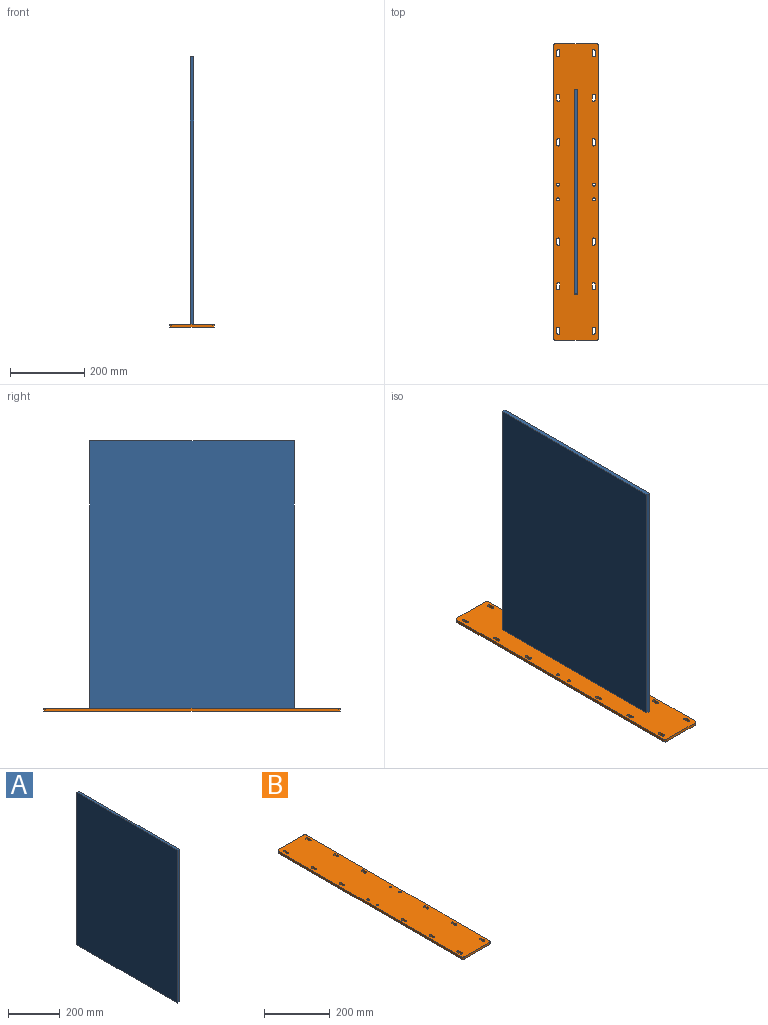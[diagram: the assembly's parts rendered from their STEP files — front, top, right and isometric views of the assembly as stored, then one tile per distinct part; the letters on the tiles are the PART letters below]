
ASSEMBLY  parts=2 mates=1
PART A: 6 faces, bbox 10x550x720 mm
  f0: plane 720x10mm, normal (0,-1,0), area 7200mm2, adj f1,f3,f4,f5
  f1: plane 550x10mm, normal (0,0,1), area 5500mm2, adj f0,f2,f4,f5
  f2: plane 720x10mm, normal (0,1,0), area 7200mm2, adj f1,f3,f4,f5
  f3: plane 550x10mm, normal (0,0,-1), area 5500mm2, adj f0,f2,f4,f5
  f4: plane 720x550mm, normal (-1,0,0), area 396000mm2, adj f0,f1,f2,f3
  f5: plane 720x550mm, normal (1,0,0), area 396000mm2, adj f0,f1,f2,f3
PART B: 62 faces, bbox 120x800x8 mm
  f0: plane 12x8mm, normal (-1,0,0), area 96mm2, adj f1,f30,f31,f32
  f1: cylinder r=4mm len=8mm, axis (0,0,-1), area 100.5mm2, adj f0,f2,f31,f32
  f2: plane 12x8mm, normal (1,0,0), area 96mm2, adj f1,f30,f31,f32
  f3: plane 12x8mm, normal (-1,0,0), area 96mm2, adj f4,f22,f31,f32
  f4: cylinder r=4mm len=8mm, axis (0,0,-1), area 100.5mm2, adj f3,f5,f31,f32
  f5: plane 12x8mm, normal (1,0,0), area 96mm2, adj f4,f22,f31,f32
  f6: plane 12x8mm, normal (-1,0,0), area 96mm2, adj f7,f23,f31,f32
  f7: cylinder r=4mm len=8mm, axis (0,0,-1), area 100.5mm2, adj f6,f8,f31,f32
  f8: plane 12x8mm, normal (1,0,0), area 96mm2, adj f7,f23,f31,f32
  f9: plane 788x8mm, normal (1,0,0), area 6304mm2, adj f10,f31,f32,f42
  f10: cylinder r=6mm len=8mm, axis (0,0,-1), area 75.4mm2, adj f9,f11,f31,f32
  f11: plane 108x8mm, normal (0,1,0), area 864mm2, adj f10,f12,f31,f32
  f12: cylinder r=6mm len=8mm, axis (0,0,-1), area 75.4mm2, adj f11,f24,f31,f32
  f13: plane 12x8mm, normal (-1,0,0), area 96mm2, adj f14,f25,f31,f32
  f14: cylinder r=4mm len=8mm, axis (0,0,-1), area 100.5mm2, adj f13,f15,f31,f32
  f15: plane 12x8mm, normal (1,0,0), area 96mm2, adj f14,f25,f31,f32
  f16: plane 12x8mm, normal (-1,0,0), area 96mm2, adj f17,f26,f31,f32
  f17: cylinder r=4mm len=8mm, axis (0,0,-1), area 100.5mm2, adj f16,f18,f31,f32
  f18: plane 12x8mm, normal (1,0,0), area 96mm2, adj f17,f26,f31,f32
  f19: plane 12x8mm, normal (-1,0,0), area 96mm2, adj f20,f27,f31,f32
  f20: cylinder r=4mm len=8mm, axis (0,0,-1), area 100.5mm2, adj f19,f21,f31,f32
  f21: plane 12x8mm, normal (1,0,0), area 96mm2, adj f20,f27,f31,f32
  f22: cylinder r=4mm len=8mm, axis (0,0,-1), area 100.5mm2, adj f3,f5,f31,f32
  f23: cylinder r=4mm len=8mm, axis (0,0,-1), area 100.5mm2, adj f6,f8,f31,f32
  f24: plane 788x8mm, normal (-1,0,0), area 6304mm2, adj f12,f31,f32,f44
  f25: cylinder r=4mm len=8mm, axis (0,0,-1), area 100.5mm2, adj f13,f15,f31,f32
  f26: cylinder r=4mm len=8mm, axis (0,0,-1), area 100.5mm2, adj f16,f18,f31,f32
  f27: cylinder r=4mm len=8mm, axis (0,0,-1), area 100.5mm2, adj f19,f21,f31,f32
  f28: cylinder r=4mm len=8mm, axis (0,0,-1), area 201.1mm2, adj f31,f32
  f29: cylinder r=4mm len=8mm, axis (0,0,-1), area 201.1mm2, adj f31,f32
  f30: cylinder r=4mm len=8mm, axis (0,0,-1), area 100.5mm2, adj f0,f2,f31,f32
  f31: plane 800x120mm, normal (0,0,1), area 94012.8mm2, adj f0,f1,f2,f3,f4,f5,f6,f7
  f32: plane 800x120mm, normal (0,0,-1), area 94012.8mm2, adj f0,f1,f2,f3,f4,f5,f6,f7
  f33: plane 12x8mm, normal (-1,0,0), area 96mm2, adj f31,f32,f34,f61
  f34: cylinder r=4mm len=8mm, axis (0,0,-1), area 100.5mm2, adj f31,f32,f33,f35
  f35: plane 12x8mm, normal (1,0,0), area 96mm2, adj f31,f32,f34,f61
  f36: plane 12x8mm, normal (-1,0,0), area 96mm2, adj f31,f32,f37,f54
  f37: cylinder r=4mm len=8mm, axis (0,0,-1), area 100.5mm2, adj f31,f32,f36,f38
  f38: plane 12x8mm, normal (1,0,0), area 96mm2, adj f31,f32,f37,f54
  f39: plane 12x8mm, normal (-1,0,0), area 96mm2, adj f31,f32,f40,f55
  f40: cylinder r=4mm len=8mm, axis (0,0,-1), area 100.5mm2, adj f31,f32,f39,f41
  f41: plane 12x8mm, normal (1,0,0), area 96mm2, adj f31,f32,f40,f55
  f42: cylinder r=6mm len=8mm, axis (0,0,-1), area 75.4mm2, adj f9,f31,f32,f43
  f43: plane 108x8mm, normal (0,-1,0), area 864mm2, adj f31,f32,f42,f44
  f44: cylinder r=6mm len=8mm, axis (0,0,-1), area 75.4mm2, adj f24,f31,f32,f43
  f45: plane 12x8mm, normal (-1,0,0), area 96mm2, adj f31,f32,f46,f56
  f46: cylinder r=4mm len=8mm, axis (0,0,-1), area 100.5mm2, adj f31,f32,f45,f47
  f47: plane 12x8mm, normal (1,0,0), area 96mm2, adj f31,f32,f46,f56
  f48: plane 12x8mm, normal (-1,0,0), area 96mm2, adj f31,f32,f49,f57
  f49: cylinder r=4mm len=8mm, axis (0,0,-1), area 100.5mm2, adj f31,f32,f48,f50
  f50: plane 12x8mm, normal (1,0,0), area 96mm2, adj f31,f32,f49,f57
  f51: plane 12x8mm, normal (-1,0,0), area 96mm2, adj f31,f32,f52,f58
  f52: cylinder r=4mm len=8mm, axis (0,0,-1), area 100.5mm2, adj f31,f32,f51,f53
  f53: plane 12x8mm, normal (1,0,0), area 96mm2, adj f31,f32,f52,f58
  f54: cylinder r=4mm len=8mm, axis (0,0,-1), area 100.5mm2, adj f31,f32,f36,f38
  f55: cylinder r=4mm len=8mm, axis (0,0,-1), area 100.5mm2, adj f31,f32,f39,f41
  f56: cylinder r=4mm len=8mm, axis (0,0,-1), area 100.5mm2, adj f31,f32,f45,f47
  f57: cylinder r=4mm len=8mm, axis (0,0,-1), area 100.5mm2, adj f31,f32,f48,f50
  f58: cylinder r=4mm len=8mm, axis (0,0,-1), area 100.5mm2, adj f31,f32,f51,f53
  f59: cylinder r=4mm len=8mm, axis (0,0,-1), area 201.1mm2, adj f31,f32
  f60: cylinder r=4mm len=8mm, axis (0,0,-1), area 201.1mm2, adj f31,f32
  f61: cylinder r=4mm len=8mm, axis (0,0,-1), area 100.5mm2, adj f31,f32,f33,f35
PLACE A t=(-832.06,-893.94,-115.38)mm
PLACE B t=(903.92,-780.95,-39.23)mm fixed
MATE planar A.f3 <-> B.f31  axis (0,0,-1) through (-2077.03,-1178.62,8.77)mm
